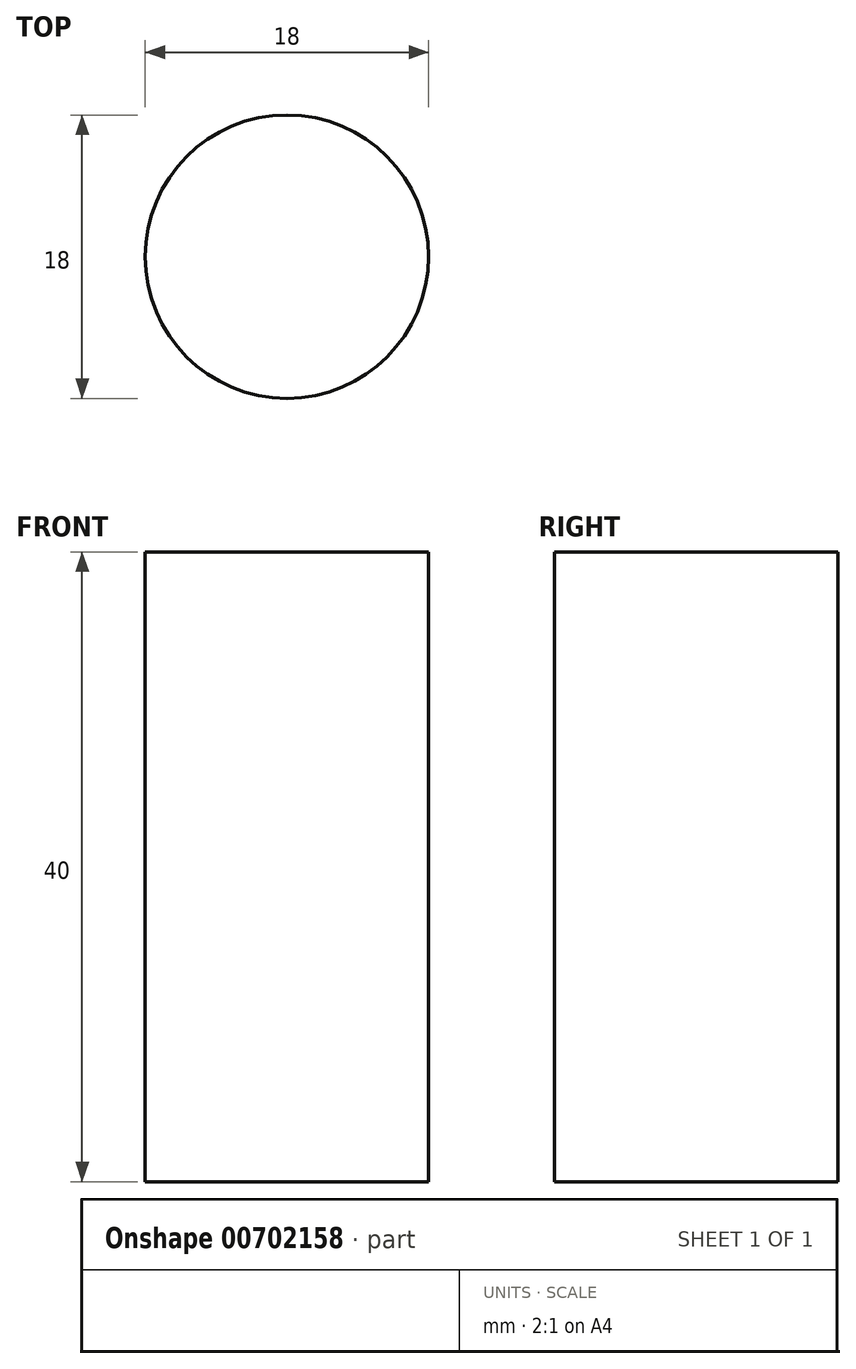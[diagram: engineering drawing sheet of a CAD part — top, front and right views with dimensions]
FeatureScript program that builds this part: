
annotation { "Feature Type Name" : "Feature", "Feature Type Description" : "" }
export const myFeature = defineFeature(function(context is Context, id is Id, definition is map)
    precondition{}
    {
        {
            var Q0;
            Q0=qCreatedBy(makeId("Top.planeOp"),FACE);
            var sketch = newSketch(context, id + "F0", { "sketchPlane" : qUnion([Q0])});
            skCircle(sketch, "E0", {"center": v(0, 0) * mm, "radius": 9 * mm});
            skSolve(sketch);
        }
        {
            var Q0;
            Q0 = qSketchRegion(id + "F0", true);
            extrude(context, id + "F1", {"entities" : qUnion([Q0]), "endBound" : BoundingType.SYMMETRIC, "depth" : 40 * mm, "offsetDistance" : 25.4 * mm});
        }
    });
